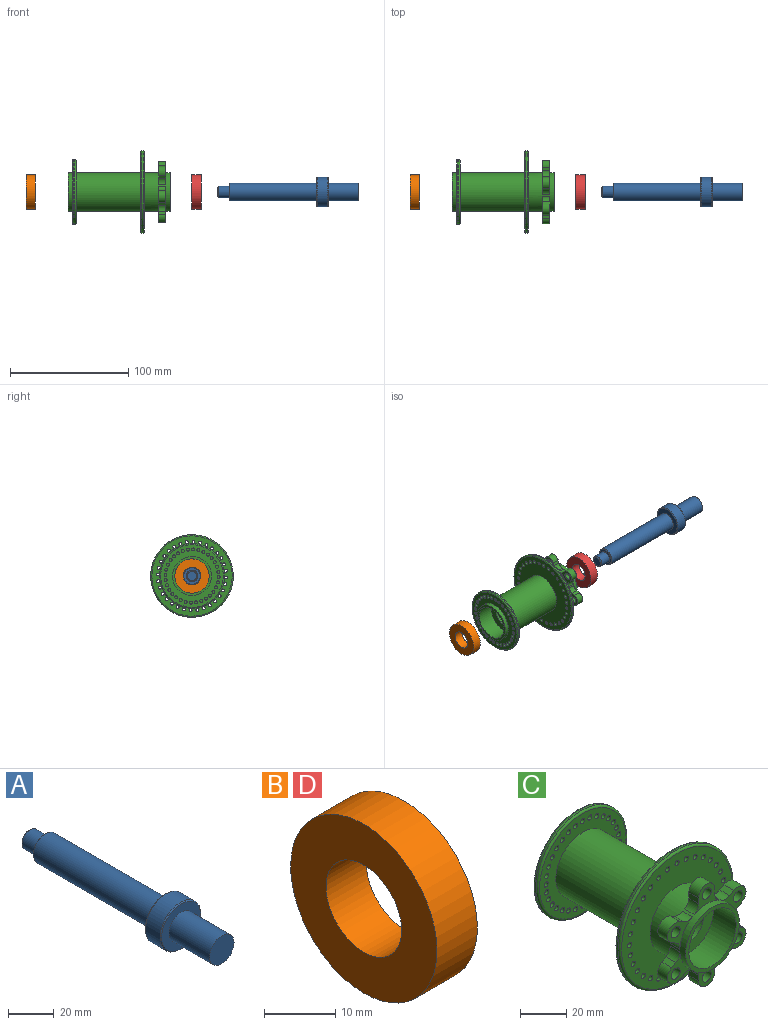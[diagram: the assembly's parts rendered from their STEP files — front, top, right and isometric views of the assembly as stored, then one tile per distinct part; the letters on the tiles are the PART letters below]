
ASSEMBLY  parts=4 mates=3
PART A: 13 faces, bbox 25x119x25 mm
  f0: cylinder r=7.5mm len=25mm, axis (0,1,0), area 1178.1mm2, adj f1,f3
  f1: plane 15x15mm, normal (0,-1,0), area 176.7mm2, adj f0
  f2: cylinder r=12.5mm len=25mm, axis (0,1,0), area 706.9mm2, adj f11,f12
  f3: plane 24x24mm, normal (0,-1,0), area 275.7mm2, adj f0,f11
  f4: plane 24x24mm, normal (0,1,0), area 275.7mm2, adj f6,f12
  f5: plane 14x14mm, normal (0,1,0), area 75.4mm2, adj f7,f10
  f6: cylinder r=7.5mm len=73.5mm, axis (0,1,0), area 3463.6mm2, adj f4,f10
  f7: cylinder r=5mm len=10mm, axis (0,-1,0), area 282.7mm2, adj f5,f9
  f8: plane 8x8mm, normal (0,1,0), area 50.3mm2, adj f9
  f9: cone r=4mm half-angle=45deg, axis (0,-1,0), area 40mm2, adj f7,f8
  f10: cone r=7.5mm half-angle=45deg, axis (0,-1,0), area 32.2mm2, adj f5,f6
  f11: cone r=12mm half-angle=45deg, axis (0,1,0), area 54.4mm2, adj f2,f3
  f12: cone r=12.5mm half-angle=45deg, axis (0,-1,0), area 54.4mm2, adj f2,f4
PART B: 4 faces, bbox 8x29x29 mm
  f0: cylinder r=7.5mm len=15mm, axis (-1,0,0), area 377mm2, adj f2,f3
  f1: cylinder r=14.5mm len=29mm, axis (-1,0,0), area 728.8mm2, adj f2,f3
  f2: plane 29x29mm, normal (1,0,0), area 483.8mm2, adj f0,f1
  f3: plane 29x29mm, normal (-1,0,0), area 483.8mm2, adj f0,f1
PART C: 132 faces, bbox 75.8x86x75.8 mm
  f0: cylinder r=16.5mm len=33mm, axis (0,1,0), area 1680.2mm2, adj f5,f11,f84,f85,f90,f91,f96,f97
  f1: cylinder r=16.5mm len=33mm, axis (0,1,0), area 362.9mm2, adj f6,f15
  f2: cylinder r=16.5mm len=54.75mm, axis (0,1,0), area 5676.1mm2, adj f12,f14
  f3: cylinder r=14.5mm len=29mm, axis (0,1,0), area 1275.5mm2, adj f6,f9
  f4: cylinder r=14.5mm len=29mm, axis (0,1,0), area 1275.5mm2, adj f5,f8
  f5: plane 33x33mm, normal (0,-1,0), area 194.8mm2, adj f0,f4
  f6: plane 33x33mm, normal (0,1,0), area 194.8mm2, adj f1,f3
  f7: cylinder r=8.5mm len=58mm, axis (0,1,0), area 3097.6mm2, adj f8,f9
  f8: plane 29x29mm, normal (0,-1,0), area 433.5mm2, adj f4,f7
  f9: plane 29x29mm, normal (0,1,0), area 433.5mm2, adj f3,f7
  f10: cylinder r=35mm len=70mm, axis (0,1,0), area 219.9mm2, adj f130,f131
  f11: plane 68x68mm, normal (0,-1,0), area 2619.3mm2, adj f0,f16,f17,f18,f19,f20,f21,f22
  f12: plane 68x68mm, normal (0,1,0), area 2619.3mm2, adj f2,f16,f17,f18,f19,f20,f21,f22
  f13: cylinder r=27.5mm len=55mm, axis (0,1,0), area 172.8mm2, adj f128,f129
  f14: plane 53x53mm, normal (0,-1,0), area 1193.8mm2, adj f2,f48,f49,f50,f51,f52,f53,f54
  f15: plane 53x53mm, normal (0,1,0), area 1193.8mm2, adj f1,f48,f49,f50,f51,f52,f53,f54
  f16: cylinder r=1.25mm len=3mm, axis (0,-1,0), area 23.6mm2, adj f11,f12
  f17: cylinder r=1.25mm len=3mm, axis (0,-1,0), area 23.6mm2, adj f11,f12
  f18: cylinder r=1.25mm len=3mm, axis (0,-1,0), area 23.6mm2, adj f11,f12
  f19: cylinder r=1.25mm len=3mm, axis (0,-1,0), area 23.6mm2, adj f11,f12
  f20: cylinder r=1.25mm len=3mm, axis (0,-1,0), area 23.6mm2, adj f11,f12
  f21: cylinder r=1.25mm len=3mm, axis (0,-1,0), area 23.6mm2, adj f11,f12
  f22: cylinder r=1.25mm len=3mm, axis (0,-1,0), area 23.6mm2, adj f11,f12
  f23: cylinder r=1.25mm len=3mm, axis (0,-1,0), area 23.6mm2, adj f11,f12
  f24: cylinder r=1.25mm len=3mm, axis (0,-1,0), area 23.6mm2, adj f11,f12
  f25: cylinder r=1.25mm len=3mm, axis (0,-1,0), area 23.6mm2, adj f11,f12
  f26: cylinder r=1.25mm len=3mm, axis (0,-1,0), area 23.6mm2, adj f11,f12
  f27: cylinder r=1.25mm len=3mm, axis (0,-1,0), area 23.6mm2, adj f11,f12
  f28: cylinder r=1.25mm len=3mm, axis (0,-1,0), area 23.6mm2, adj f11,f12
  f29: cylinder r=1.25mm len=3mm, axis (0,-1,0), area 23.6mm2, adj f11,f12
  f30: cylinder r=1.25mm len=3mm, axis (0,-1,0), area 23.6mm2, adj f11,f12
  f31: cylinder r=1.25mm len=3mm, axis (0,-1,0), area 23.6mm2, adj f11,f12
  f32: cylinder r=1.25mm len=3mm, axis (0,-1,0), area 23.6mm2, adj f11,f12
  f33: cylinder r=1.25mm len=3mm, axis (0,-1,0), area 23.6mm2, adj f11,f12
  f34: cylinder r=1.25mm len=3mm, axis (0,-1,0), area 23.6mm2, adj f11,f12
  f35: cylinder r=1.25mm len=3mm, axis (0,-1,0), area 23.6mm2, adj f11,f12
  f36: cylinder r=1.25mm len=3mm, axis (0,-1,0), area 23.6mm2, adj f11,f12
  f37: cylinder r=1.25mm len=3mm, axis (0,-1,0), area 23.6mm2, adj f11,f12
  f38: cylinder r=1.25mm len=3mm, axis (0,-1,0), area 23.6mm2, adj f11,f12
  f39: cylinder r=1.25mm len=3mm, axis (0,-1,0), area 23.6mm2, adj f11,f12
  f40: cylinder r=1.25mm len=3mm, axis (0,-1,0), area 23.6mm2, adj f11,f12
  f41: cylinder r=1.25mm len=3mm, axis (0,-1,0), area 23.6mm2, adj f11,f12
  f42: cylinder r=1.25mm len=3mm, axis (0,-1,0), area 23.6mm2, adj f11,f12
  f43: cylinder r=1.25mm len=3mm, axis (0,-1,0), area 23.6mm2, adj f11,f12
  f44: cylinder r=1.25mm len=3mm, axis (0,-1,0), area 23.6mm2, adj f11,f12
  f45: cylinder r=1.25mm len=3mm, axis (0,-1,0), area 23.6mm2, adj f11,f12
  f46: cylinder r=1.25mm len=3mm, axis (0,-1,0), area 23.6mm2, adj f11,f12
  f47: cylinder r=1.25mm len=3mm, axis (0,-1,0), area 23.6mm2, adj f11,f12
  f48: cylinder r=1.25mm len=3mm, axis (0,1,0), area 23.6mm2, adj f14,f15
  f49: cylinder r=1.25mm len=3mm, axis (0,1,0), area 23.6mm2, adj f14,f15
  f50: cylinder r=1.25mm len=3mm, axis (0,1,0), area 23.6mm2, adj f14,f15
  f51: cylinder r=1.25mm len=3mm, axis (0,1,0), area 23.6mm2, adj f14,f15
  f52: cylinder r=1.25mm len=3mm, axis (0,1,0), area 23.6mm2, adj f14,f15
  f53: cylinder r=1.25mm len=3mm, axis (0,1,0), area 23.6mm2, adj f14,f15
  f54: cylinder r=1.25mm len=3mm, axis (0,1,0), area 23.6mm2, adj f14,f15
  f55: cylinder r=1.25mm len=3mm, axis (0,1,0), area 23.6mm2, adj f14,f15
  f56: cylinder r=1.25mm len=3mm, axis (0,1,0), area 23.6mm2, adj f14,f15
  f57: cylinder r=1.25mm len=3mm, axis (0,1,0), area 23.6mm2, adj f14,f15
  f58: cylinder r=1.25mm len=3mm, axis (0,1,0), area 23.6mm2, adj f14,f15
  f59: cylinder r=1.25mm len=3mm, axis (0,1,0), area 23.6mm2, adj f14,f15
  f60: cylinder r=1.25mm len=3mm, axis (0,1,0), area 23.6mm2, adj f14,f15
  f61: cylinder r=1.25mm len=3mm, axis (0,1,0), area 23.6mm2, adj f14,f15
  f62: cylinder r=1.25mm len=3mm, axis (0,1,0), area 23.6mm2, adj f14,f15
  f63: cylinder r=1.25mm len=3mm, axis (0,1,0), area 23.6mm2, adj f14,f15
  f64: cylinder r=1.25mm len=3mm, axis (0,1,0), area 23.6mm2, adj f14,f15
  f65: cylinder r=1.25mm len=3mm, axis (0,1,0), area 23.6mm2, adj f14,f15
  f66: cylinder r=1.25mm len=3mm, axis (0,1,0), area 23.6mm2, adj f14,f15
  f67: cylinder r=1.25mm len=3mm, axis (0,1,0), area 23.6mm2, adj f14,f15
  f68: cylinder r=1.25mm len=3mm, axis (0,1,0), area 23.6mm2, adj f14,f15
  f69: cylinder r=1.25mm len=3mm, axis (0,1,0), area 23.6mm2, adj f14,f15
  f70: cylinder r=1.25mm len=3mm, axis (0,1,0), area 23.6mm2, adj f14,f15
  f71: cylinder r=1.25mm len=3mm, axis (0,1,0), area 23.6mm2, adj f14,f15
  f72: cylinder r=1.25mm len=3mm, axis (0,1,0), area 23.6mm2, adj f14,f15
  f73: cylinder r=1.25mm len=3mm, axis (0,1,0), area 23.6mm2, adj f14,f15
  f74: cylinder r=1.25mm len=3mm, axis (0,1,0), area 23.6mm2, adj f14,f15
  f75: cylinder r=1.25mm len=3mm, axis (0,1,0), area 23.6mm2, adj f14,f15
  f76: cylinder r=1.25mm len=3mm, axis (0,1,0), area 23.6mm2, adj f14,f15
  f77: cylinder r=1.25mm len=3mm, axis (0,1,0), area 23.6mm2, adj f14,f15
  f78: cylinder r=1.25mm len=3mm, axis (0,1,0), area 23.6mm2, adj f14,f15
  f79: cylinder r=1.25mm len=3mm, axis (0,1,0), area 23.6mm2, adj f14,f15
  f80: cylinder r=5mm len=9.33mm, axis (0,-1,0), area 94.2mm2, adj f81,f82,f84,f85
  f81: plane 6x2.57mm, normal (0.5,0,0.87), area 17.8mm2, adj f80,f84,f85,f118
  f82: plane 6x2.57mm, normal (-0.5,0,-0.87), area 17.8mm2, adj f80,f84,f85,f121
  f83: cylinder r=2.75mm len=6mm, axis (0,-1,0), area 103.7mm2, adj f84,f85
  f84: plane 15.34x15.24mm, normal (0,1,0), area 76.6mm2, adj f0,f80,f81,f82,f83,f118,f121
  f85: plane 15.34x15.24mm, normal (0,-1,0), area 76.6mm2, adj f0,f80,f81,f82,f83,f118,f121
  f86: cylinder r=5mm len=9.33mm, axis (0,-1,0), area 94.2mm2, adj f87,f89,f90,f91
  f87: plane 6x2.57mm, normal (-0.5,0,0.87), area 17.8mm2, adj f86,f90,f91,f117
  f88: cylinder r=2.75mm len=6mm, axis (0,-1,0), area 103.7mm2, adj f90,f91
  f89: plane 6x2.57mm, normal (0.5,0,-0.87), area 17.8mm2, adj f86,f90,f91,f119
  f90: plane 15.34x15.24mm, normal (0,1,0), area 76.6mm2, adj f0,f86,f87,f88,f89,f117,f119
  f91: plane 15.34x15.24mm, normal (0,-1,0), area 76.6mm2, adj f0,f86,f87,f88,f89,f117,f119
  f92: cylinder r=5mm len=10mm, axis (0,-1,0), area 94.2mm2, adj f93,f95,f96,f97
  f93: plane 6x2.97mm, normal (-1,0,0), area 17.8mm2, adj f92,f96,f97,f126
  f94: cylinder r=2.75mm len=6mm, axis (0,-1,0), area 103.7mm2, adj f96,f97
  f95: plane 6x2.97mm, normal (1,0,0), area 17.8mm2, adj f92,f96,f97,f116
  f96: plane 15.35x12.39mm, normal (0,1,0), area 76.6mm2, adj f0,f92,f93,f94,f95,f116,f126
  f97: plane 15.35x12.39mm, normal (0,-1,0), area 76.6mm2, adj f0,f92,f93,f94,f95,f116,f126
  f98: cylinder r=5mm len=9.33mm, axis (0,-1,0), area 94.2mm2, adj f99,f101,f102,f103
  f99: plane 6x2.57mm, normal (-0.5,0,-0.87), area 17.8mm2, adj f98,f102,f103,f124
  f100: cylinder r=2.75mm len=6mm, axis (0,-1,0), area 103.7mm2, adj f102,f103
  f101: plane 6x2.57mm, normal (0.5,0,0.87), area 17.8mm2, adj f98,f102,f103,f127
  f102: plane 15.34x15.24mm, normal (0,1,0), area 76.6mm2, adj f0,f98,f99,f100,f101,f124,f127
  f103: plane 15.34x15.24mm, normal (0,-1,0), area 76.6mm2, adj f0,f98,f99,f100,f101,f124,f127
  f104: cylinder r=5mm len=9.33mm, axis (0,-1,0), area 94.2mm2, adj f105,f107,f108,f109
  f105: plane 6x2.57mm, normal (0.5,0,-0.87), area 17.8mm2, adj f104,f108,f109,f122
  f106: cylinder r=2.75mm len=6mm, axis (0,-1,0), area 103.7mm2, adj f108,f109
  f107: plane 6x2.57mm, normal (-0.5,0,0.87), area 17.8mm2, adj f104,f108,f109,f125
  f108: plane 15.34x15.24mm, normal (0,1,0), area 76.6mm2, adj f0,f104,f105,f106,f107,f122,f125
  f109: plane 15.34x15.24mm, normal (0,-1,0), area 76.6mm2, adj f0,f104,f105,f106,f107,f122,f125
  f110: cylinder r=5mm len=10mm, axis (0,-1,0), area 94.2mm2, adj f111,f113,f114,f115
  f111: plane 6x2.97mm, normal (1,0,0), area 17.8mm2, adj f110,f114,f115,f120
  f112: cylinder r=2.75mm len=6mm, axis (0,-1,0), area 103.7mm2, adj f114,f115
  f113: plane 6x2.97mm, normal (-1,0,0), area 17.8mm2, adj f110,f114,f115,f123
  f114: plane 15.35x12.39mm, normal (0,1,0), area 76.6mm2, adj f0,f110,f111,f112,f113,f120,f123
  f115: plane 15.35x12.39mm, normal (0,-1,0), area 76.6mm2, adj f0,f110,f111,f112,f113,f120,f123
  f116: cylinder r=5mm len=6mm, axis (0,1,0), area 32.6mm2, adj f0,f95,f96,f97
  f117: cylinder r=5mm len=6mm, axis (0,1,0), area 32.6mm2, adj f0,f87,f90,f91
  f118: cylinder r=5mm len=6mm, axis (0,1,0), area 32.6mm2, adj f0,f81,f84,f85
  f119: cylinder r=5mm len=6mm, axis (0,1,0), area 32.6mm2, adj f0,f89,f90,f91
  f120: cylinder r=5mm len=6mm, axis (0,1,0), area 32.6mm2, adj f0,f111,f114,f115
  f121: cylinder r=5mm len=6mm, axis (0,1,0), area 32.6mm2, adj f0,f82,f84,f85
  f122: cylinder r=5mm len=6mm, axis (0,1,0), area 32.6mm2, adj f0,f105,f108,f109
  f123: cylinder r=5mm len=6mm, axis (0,1,0), area 32.6mm2, adj f0,f113,f114,f115
  f124: cylinder r=5mm len=6mm, axis (0,1,0), area 32.6mm2, adj f0,f99,f102,f103
  f125: cylinder r=5mm len=6mm, axis (0,1,0), area 32.6mm2, adj f0,f107,f108,f109
  f126: cylinder r=5mm len=6mm, axis (0,1,0), area 32.6mm2, adj f0,f93,f96,f97
  f127: cylinder r=5mm len=6mm, axis (0,1,0), area 32.6mm2, adj f0,f101,f102,f103
  f128: torus R=26.5mm, axis (0,-1,0), area 267.8mm2, adj f13,f15
  f129: torus R=26.5mm, axis (0,-1,0), area 267.8mm2, adj f13,f14
  f130: torus R=34mm, axis (0,-1,0), area 341.8mm2, adj f10,f12
  f131: torus R=34mm, axis (0,-1,0), area 341.8mm2, adj f10,f11
PART D: same geometry as B
PLACE A rot(axis=(-0.63,0.63,0.44),132.1deg) t=(67.08,-60.87,-2.85)mm
PLACE B rot(axis=(1,0,0),70deg) t=(-184.09,-60.87,-2.85)mm
PLACE C rot(axis=(0.7,-0.7,0.12),165.9deg) t=(-105.1,-60.87,-2.85)mm
PLACE D rot(axis=(1,0,0),70deg) t=(-43.67,-60.87,-2.85)mm
MATE cylindrical C.f3 <-> B.f1  axis (-1,0,0) through (-148.1,-60.87,-2.85)mm
MATE cylindrical C.f3 <-> D.f1  axis (-1,0,0) through (-62.1,-60.87,-2.85)mm
MATE cylindrical A.f0 <-> D.f0  axis (-1,0,0) through (25.33,-60.87,-2.85)mm
